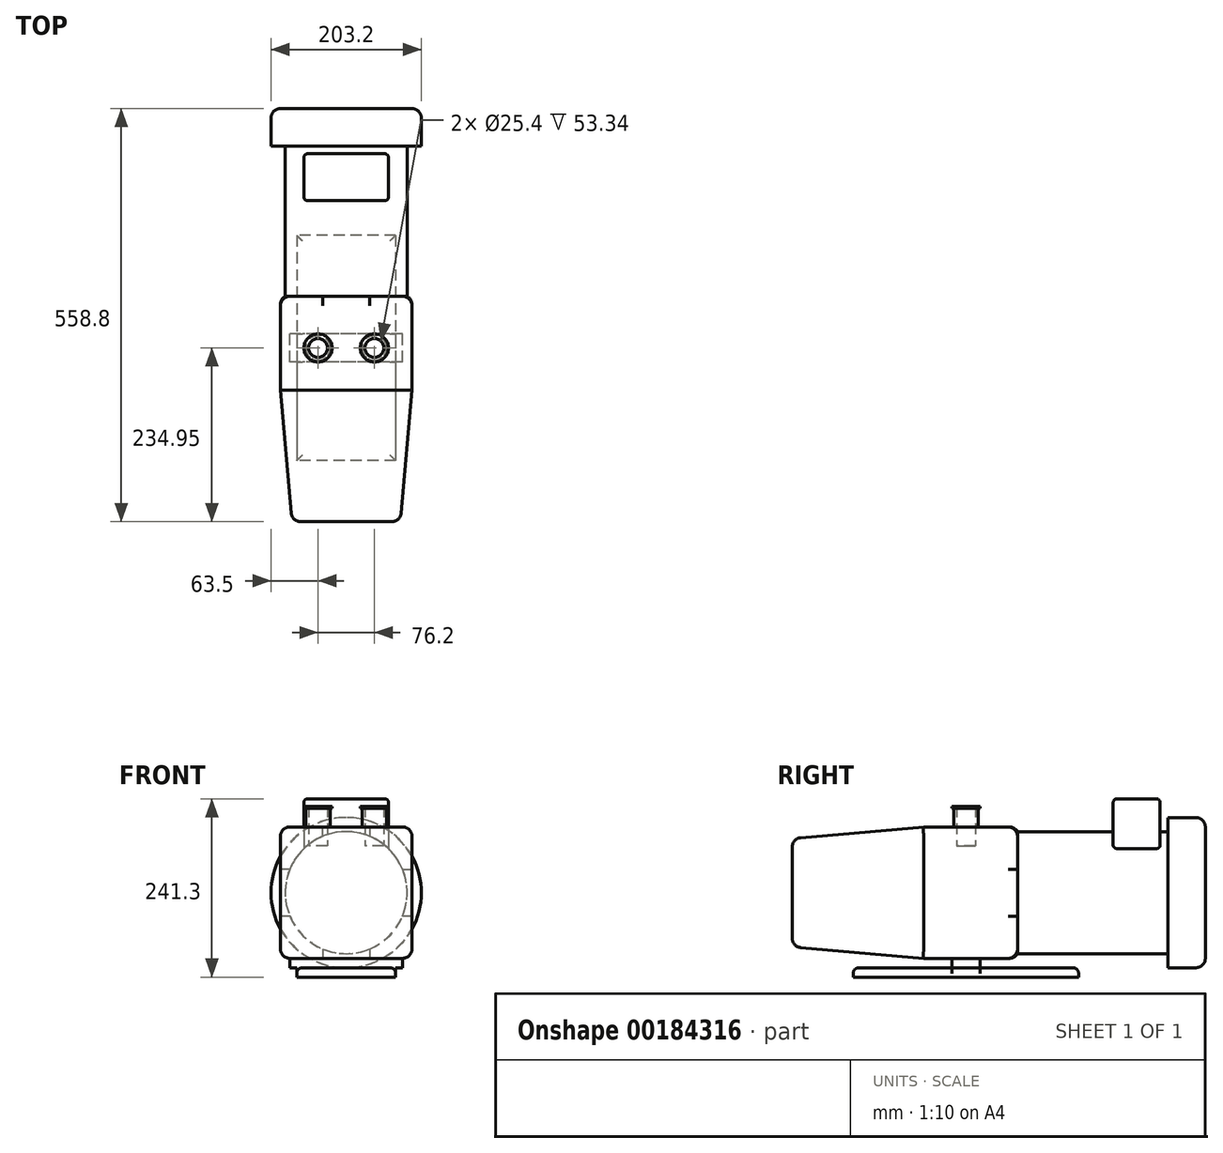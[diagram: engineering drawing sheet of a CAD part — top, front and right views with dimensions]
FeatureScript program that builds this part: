
annotation { "Feature Type Name" : "Feature", "Feature Type Description" : "" }
export const myFeature = defineFeature(function(context is Context, id is Id, definition is map)
    precondition{}
    {
        {
            var Q0;
            Q0=qCreatedBy(makeId("Front.planeOp"),FACE);
            var sketch = newSketch(context, id + "F0", { "sketchPlane" : qUnion([Q0])});
            skLineSegment(sketch, "E0.bottom", {"start": v(88.9, -88.9) * mm, "end": v(-88.9, -88.9) * mm});
            skLineSegment(sketch, "E0.top", {"start": v(88.9, 88.9) * mm, "end": v(-88.9, 88.9) * mm});
            skLineSegment(sketch, "E0.left", {"start": v(88.9, -88.9) * mm, "end": v(88.9, 88.9) * mm});
            skLineSegment(sketch, "E0.right", {"start": v(-88.9, -88.9) * mm, "end": v(-88.9, 88.9) * mm});
            skPoint(sketch, "E0.middle", {"position": v(0, 0) * mm});
            skSolve(sketch);
        }
        {
            var Q0;
            Q0=makeQuery(id+"F0.imprint","IMPRINT",FACE,{"disambiguationData":[TD([[makeQuery(id+"F0.imprint","IMPRINT",EDGE,{"derivedFrom":sQuery(id+"F0.wireOp",EDGE,"E0.bottom")}),-1.0]])]});
            extrude(context, id + "F1", {"entities" : qUnion([Q0]), "depth" : 127 * mm});
        }
        {
            var Q0;
            Q0=makeQuery(id+"F1.opExtrude","CAP_FACE",FACE,{"disambiguationData":[OSD([sQuery(id+"F0.wireOp",EDGE,"E0.bottom"),sQuery(id+"F0.wireOp",EDGE,"E0.top"),sQuery(id+"F0.wireOp",EDGE,"E0.left"),sQuery(id+"F0.wireOp",EDGE,"E0.right")])],"isStart":false});
            var sketch = newSketch(context, id + "F2", { "sketchPlane" : qUnion([Q0])});
            skLineSegment(sketch, "E1.bottom", {"start": v(88.9, -88.9) * mm, "end": v(-88.9, -88.9) * mm});
            skLineSegment(sketch, "E1.top", {"start": v(88.9, 88.9) * mm, "end": v(-88.9, 88.9) * mm});
            skLineSegment(sketch, "E1.left", {"start": v(88.9, -88.9) * mm, "end": v(88.9, 88.9) * mm});
            skLineSegment(sketch, "E1.right", {"start": v(-88.9, -88.9) * mm, "end": v(-88.9, 88.9) * mm});
            skPoint(sketch, "E1.middle", {"position": v(0, 0) * mm});
            skSolve(sketch);
        }
        {
            var Q0;
            Q0 = qSketchRegion(id + "F2", true);
            extrude(context, id + "F3", {"entities" : qUnion([Q0]), "operationType" : NewBodyOperationType.ADD, "depth" : 177.8 * mm, "hasDraft" : true, "draftAngle" : 5 * degree, "draftPullDirection" : true});
        }
        {
            var Q0;
            Q0=makeQuery(id+"F1.opExtrude","CAP_FACE",FACE,{"disambiguationData":[OSD([sQuery(id+"F0.wireOp",EDGE,"E0.bottom"),sQuery(id+"F0.wireOp",EDGE,"E0.top"),sQuery(id+"F0.wireOp",EDGE,"E0.left"),sQuery(id+"F0.wireOp",EDGE,"E0.right")])],"isStart":true});
            var sketch = newSketch(context, id + "F4", { "sketchPlane" : qUnion([Q0])});
            skCircle(sketch, "E2", {"center": v(0, 0) * mm, "radius": 82.55 * mm});
            skSolve(sketch);
        }
        {
            var Q0;
            Q0 = qSketchRegion(id + "F4", true);
            extrude(context, id + "F5", {"entities" : qUnion([Q0]), "operationType" : NewBodyOperationType.ADD, "depth" : 203.2 * mm});
        }
        {
            var Q0;
            Q0=makeQuery(id+"F5.opExtrude","CAP_FACE",FACE,{"disambiguationData":[OSD([sQuery(id+"F4.wireOp",EDGE,"E2")])],"isStart":false});
            var sketch = newSketch(context, id + "F6", { "sketchPlane" : qUnion([Q0])});
            skCircle(sketch, "E3", {"center": v(0, 0) * mm, "radius": 101.6 * mm});
            skSolve(sketch);
        }
        {
            var Q0;
            Q0 = qSketchRegion(id + "F6", true);
            extrude(context, id + "F7", {"entities" : qUnion([Q0]), "operationType" : NewBodyOperationType.ADD, "depth" : 50.8 * mm});
        }
        {
            var Q0;
            Q0=makeQuery(id+"F3.opExtrude","SWEPT_EDGE",EDGE,{"disambiguationData":[OSD([sQuery(id+"F2.wireOp",EDGE,"E1.top"),sQuery(id+"F2.wireOp",EDGE,"E1.left")])]});
            var Q1;
            Q1=makeQuery(id+"F3.opExtrude","SWEPT_EDGE",EDGE,{"disambiguationData":[OSD([sQuery(id+"F2.wireOp",EDGE,"E1.top"),sQuery(id+"F2.wireOp",EDGE,"E1.right")])]});
            var Q2;
            Q2=makeQuery(id+"F1.opExtrude","SWEPT_EDGE",EDGE,{"disambiguationData":[OSD([sQuery(id+"F0.wireOp",EDGE,"E0.top"),sQuery(id+"F0.wireOp",EDGE,"E0.left")])]});
            var Q3;
            Q3=makeQuery(id+"F1.opExtrude","CAP_EDGE",EDGE,{"disambiguationData":[OSD([sQuery(id+"F0.wireOp",EDGE,"E0.left")])],"isStart":true});
            var Q4;
            Q4=makeQuery(id+"F1.opExtrude","SWEPT_EDGE",EDGE,{"disambiguationData":[OSD([sQuery(id+"F0.wireOp",EDGE,"E0.bottom"),sQuery(id+"F0.wireOp",EDGE,"E0.left")])]});
            var Q5;
            Q5=makeQuery(id+"F3.opExtrude","SWEPT_EDGE",EDGE,{"disambiguationData":[OSD([sQuery(id+"F2.wireOp",EDGE,"E1.bottom"),sQuery(id+"F2.wireOp",EDGE,"E1.left")])]});
            var Q6;
            Q6=makeQuery(id+"F3.opExtrude","CAP_EDGE",EDGE,{"disambiguationData":[OSD([sQuery(id+"F2.wireOp",EDGE,"E1.left")])],"isStart":false});
            var Q7;
            Q7=makeQuery(id+"F3.opExtrude","CAP_EDGE",EDGE,{"disambiguationData":[OSD([sQuery(id+"F2.wireOp",EDGE,"E1.top")])],"isStart":false});
            var Q8;
            Q8=makeQuery(id+"F3.opExtrude","CAP_EDGE",EDGE,{"disambiguationData":[OSD([sQuery(id+"F2.wireOp",EDGE,"E1.right")])],"isStart":false});
            var Q9;
            Q9=makeQuery(id+"F3.opExtrude","CAP_EDGE",EDGE,{"disambiguationData":[OSD([sQuery(id+"F2.wireOp",EDGE,"E1.bottom")])],"isStart":false});
            var Q10;
            Q10=makeQuery(id+"F3.opExtrude","SWEPT_EDGE",EDGE,{"disambiguationData":[OSD([sQuery(id+"F2.wireOp",EDGE,"E1.bottom"),sQuery(id+"F2.wireOp",EDGE,"E1.right")])]});
            var Q11;
            Q11=makeQuery(id+"F1.opExtrude","CAP_EDGE",EDGE,{"disambiguationData":[OSD([sQuery(id+"F0.wireOp",EDGE,"E0.right")])],"isStart":true});
            var Q12;
            Q12=makeQuery(id+"F1.opExtrude","CAP_EDGE",EDGE,{"disambiguationData":[OSD([sQuery(id+"F0.wireOp",EDGE,"E0.top")])],"isStart":true});
            var Q13;
            Q13=makeQuery(id+"F1.opExtrude","SWEPT_EDGE",EDGE,{"disambiguationData":[OSD([sQuery(id+"F0.wireOp",EDGE,"E0.bottom"),sQuery(id+"F0.wireOp",EDGE,"E0.right")])]});
            var Q14;
            Q14=makeQuery(id+"F1.opExtrude","CAP_EDGE",EDGE,{"disambiguationData":[OSD([sQuery(id+"F0.wireOp",EDGE,"E0.bottom")])],"isStart":true});
            var Q15;
            Q15=makeQuery(id+"F1.opExtrude","SWEPT_EDGE",EDGE,{"disambiguationData":[OSD([sQuery(id+"F0.wireOp",EDGE,"E0.top"),sQuery(id+"F0.wireOp",EDGE,"E0.right")])]});
            fillet(context, id + "F8", {"entities" : qUnion([Q0, Q1, Q2, Q3, Q4, Q5, Q6, Q7, Q8, Q9, Q10, Q11, Q12, Q13, Q14, Q15]), "radius" : 12.7 * mm, "tangentPropagation" : true, "allowEdgeOverflow" : false});
        }
        {
            var Q0;
            Q0=makeQuery(id+"F7.opExtrude","CAP_EDGE",EDGE,{"disambiguationData":[OSD([sQuery(id+"F6.wireOp",EDGE,"E3")])],"isStart":false});
            fillet(context, id + "F9", {"entities" : qUnion([Q0]), "radius" : 12.7 * mm, "tangentPropagation" : true, "allowEdgeOverflow" : false});
        }
        {
            var Q0;
            Q0=makeQuery(id+"F1.opExtrude","SWEPT_FACE",FACE,{"disambiguationData":[OSD([sQuery(id+"F0.wireOp",EDGE,"E0.bottom")])]});
            var sketch = newSketch(context, id + "F10", { "sketchPlane" : qUnion([Q0])});
            skLineSegment(sketch, "E4.bottom", {"start": v(76.2, 50.8) * mm, "end": v(-76.2, 50.8) * mm});
            skLineSegment(sketch, "E4.top", {"start": v(76.2, 88.9) * mm, "end": v(-76.2, 88.9) * mm});
            skLineSegment(sketch, "E4.left", {"start": v(76.2, 50.8) * mm, "end": v(76.2, 88.9) * mm});
            skLineSegment(sketch, "E4.right", {"start": v(-76.2, 50.8) * mm, "end": v(-76.2, 88.9) * mm});
            skPoint(sketch, "E4.middle", {"position": v(0, 69.85) * mm});
            skSolve(sketch);
        }
        {
            var Q0;
            Q0 = qSketchRegion(id + "F10", true);
            extrude(context, id + "F11", {"entities" : qUnion([Q0]), "operationType" : NewBodyOperationType.ADD, "depth" : 12.7 * mm});
        }
        {
            var Q0;
            Q0=makeQuery(id+"F11.opExtrude","CAP_FACE",FACE,{"disambiguationData":[OSD([sQuery(id+"F10.wireOp",EDGE,"E4.bottom"),sQuery(id+"F10.wireOp",EDGE,"E4.top"),sQuery(id+"F10.wireOp",EDGE,"E4.left"),sQuery(id+"F10.wireOp",EDGE,"E4.right")])],"isStart":false});
            var sketch = newSketch(context, id + "F12", { "sketchPlane" : qUnion([Q0])});
            skLineSegment(sketch, "E5.bottom", {"start": v(66.88, -82.55) * mm, "end": v(-66.88, -82.55) * mm});
            skLineSegment(sketch, "E5.top", {"start": v(66.88, 222.25) * mm, "end": v(-66.88, 222.25) * mm});
            skLineSegment(sketch, "E5.left", {"start": v(66.88, -82.55) * mm, "end": v(66.88, 222.25) * mm});
            skLineSegment(sketch, "E5.right", {"start": v(-66.88, -82.55) * mm, "end": v(-66.88, 222.25) * mm});
            skPoint(sketch, "E5.middle", {"position": v(0, 69.85) * mm});
            skPoint(sketch, "E5.middle.positionSnap0", {"position": v(0, 88.9) * mm});
            skPoint(sketch, "E5.centerSnap0", {"position": v(0, 88.9) * mm});
            skSolve(sketch);
        }
        {
            var Q0;
            Q0 = qSketchRegion(id + "F12", true);
            extrude(context, id + "F13", {"entities" : qUnion([Q0]), "operationType" : NewBodyOperationType.ADD, "depth" : 12.7 * mm});
        }
        {
            var Q0;
            {var subQ0=sQuery(id+"F12.wireOp",EDGE,"E5.right");var subQ1=sQuery(id+"F12.wireOp",EDGE,"E5.bottom");var subQ2=sQuery(id+"F10.wireOp",EDGE,"E4.bottom");Q0=makeQuery(id+"F13.boolean.opBoolean","SPLIT",EDGE,{"disambiguationData":[TD([makeQuery(id+"F11.opExtrude","SWEPT_FACE",FACE,{"disambiguationData":[OSD([subQ2])]}),makeQuery(id+"F11.opExtrude","CAP_FACE",FACE,{"disambiguationData":[OSD([subQ2,sQuery(id+"F10.wireOp",EDGE,"E4.top"),sQuery(id+"F10.wireOp",EDGE,"E4.left"),sQuery(id+"F10.wireOp",EDGE,"E4.right")])],"isStart":false}),makeQuery(id+"F13.opExtrude","SWEPT_FACE",FACE,{"disambiguationData":[OSD([subQ1])]}),makeQuery(id+"F13.opExtrude","CAP_FACE",FACE,{"disambiguationData":[OSD([subQ1,sQuery(id+"F12.wireOp",EDGE,"E5.top"),sQuery(id+"F12.wireOp",EDGE,"E5.left"),subQ0])],"isStart":true}),makeQuery(id+"F13.opExtrude","SWEPT_FACE",FACE,{"disambiguationData":[OSD([subQ0])]})])],"derivedFrom":makeQuery(id+"F13.opExtrude","CAP_EDGE",EDGE,{"disambiguationData":[OSD([subQ0])],"isStart":true})});}
            var Q1;
            {var subQ0=sQuery(id+"F12.wireOp",EDGE,"E5.top");var subQ1=sQuery(id+"F12.wireOp",EDGE,"E5.right");var subQ2=sQuery(id+"F10.wireOp",EDGE,"E4.top");Q1=makeQuery(id+"F13.boolean.opBoolean","SPLIT",EDGE,{"disambiguationData":[TD([makeQuery(id+"F11.opExtrude","CAP_FACE",FACE,{"disambiguationData":[OSD([sQuery(id+"F10.wireOp",EDGE,"E4.bottom"),subQ2,sQuery(id+"F10.wireOp",EDGE,"E4.left"),sQuery(id+"F10.wireOp",EDGE,"E4.right")])],"isStart":false}),makeQuery(id+"F11.opExtrude","SWEPT_FACE",FACE,{"disambiguationData":[OSD([subQ2])]}),makeQuery(id+"F13.opExtrude","CAP_FACE",FACE,{"disambiguationData":[OSD([sQuery(id+"F12.wireOp",EDGE,"E5.bottom"),subQ0,sQuery(id+"F12.wireOp",EDGE,"E5.left"),subQ1])],"isStart":true}),makeQuery(id+"F13.opExtrude","SWEPT_FACE",FACE,{"disambiguationData":[OSD([subQ0])]}),makeQuery(id+"F13.opExtrude","SWEPT_FACE",FACE,{"disambiguationData":[OSD([subQ1])]})])],"derivedFrom":makeQuery(id+"F13.opExtrude","CAP_EDGE",EDGE,{"disambiguationData":[OSD([subQ1])],"isStart":true})});}
            var Q2;
            Q2=makeQuery(id+"F13.opExtrude","CAP_EDGE",EDGE,{"disambiguationData":[OSD([sQuery(id+"F12.wireOp",EDGE,"E5.bottom")])],"isStart":true});
            var Q3;
            Q3=makeQuery(id+"F13.opExtrude","CAP_EDGE",EDGE,{"disambiguationData":[OSD([sQuery(id+"F12.wireOp",EDGE,"E5.top")])],"isStart":true});
            var Q4;
            {var subQ0=sQuery(id+"F12.wireOp",EDGE,"E5.left");var subQ1=sQuery(id+"F12.wireOp",EDGE,"E5.bottom");var subQ2=sQuery(id+"F10.wireOp",EDGE,"E4.bottom");Q4=makeQuery(id+"F13.boolean.opBoolean","SPLIT",EDGE,{"disambiguationData":[TD([makeQuery(id+"F11.opExtrude","SWEPT_FACE",FACE,{"disambiguationData":[OSD([subQ2])]}),makeQuery(id+"F11.opExtrude","CAP_FACE",FACE,{"disambiguationData":[OSD([subQ2,sQuery(id+"F10.wireOp",EDGE,"E4.top"),sQuery(id+"F10.wireOp",EDGE,"E4.left"),sQuery(id+"F10.wireOp",EDGE,"E4.right")])],"isStart":false}),makeQuery(id+"F13.opExtrude","SWEPT_FACE",FACE,{"disambiguationData":[OSD([subQ1])]}),makeQuery(id+"F13.opExtrude","CAP_FACE",FACE,{"disambiguationData":[OSD([subQ1,sQuery(id+"F12.wireOp",EDGE,"E5.top"),subQ0,sQuery(id+"F12.wireOp",EDGE,"E5.right")])],"isStart":true}),makeQuery(id+"F13.opExtrude","SWEPT_FACE",FACE,{"disambiguationData":[OSD([subQ0])]})])],"derivedFrom":makeQuery(id+"F13.opExtrude","CAP_EDGE",EDGE,{"disambiguationData":[OSD([subQ0])],"isStart":true})});}
            var Q5;
            {var subQ0=sQuery(id+"F12.wireOp",EDGE,"E5.top");var subQ1=sQuery(id+"F12.wireOp",EDGE,"E5.left");var subQ2=sQuery(id+"F10.wireOp",EDGE,"E4.top");Q5=makeQuery(id+"F13.boolean.opBoolean","SPLIT",EDGE,{"disambiguationData":[TD([makeQuery(id+"F11.opExtrude","CAP_FACE",FACE,{"disambiguationData":[OSD([sQuery(id+"F10.wireOp",EDGE,"E4.bottom"),subQ2,sQuery(id+"F10.wireOp",EDGE,"E4.left"),sQuery(id+"F10.wireOp",EDGE,"E4.right")])],"isStart":false}),makeQuery(id+"F11.opExtrude","SWEPT_FACE",FACE,{"disambiguationData":[OSD([subQ2])]}),makeQuery(id+"F13.opExtrude","CAP_FACE",FACE,{"disambiguationData":[OSD([sQuery(id+"F12.wireOp",EDGE,"E5.bottom"),subQ0,subQ1,sQuery(id+"F12.wireOp",EDGE,"E5.right")])],"isStart":true}),makeQuery(id+"F13.opExtrude","SWEPT_FACE",FACE,{"disambiguationData":[OSD([subQ0])]}),makeQuery(id+"F13.opExtrude","SWEPT_FACE",FACE,{"disambiguationData":[OSD([subQ1])]})])],"derivedFrom":makeQuery(id+"F13.opExtrude","CAP_EDGE",EDGE,{"disambiguationData":[OSD([subQ1])],"isStart":true})});}
            fillet(context, id + "F14", {"entities" : qUnion([Q0, Q1, Q2, Q3, Q4, Q5]), "radius" : 7.62 * mm, "tangentPropagation" : true, "allowEdgeOverflow" : false});
        }
        {
            var Q0;
            Q0=qCreatedBy(makeId("Top.planeOp"),FACE);
            cPlane(context, id + "F15", {"entities" : qUnion([Q0]), "cplaneType" : CPlaneType.OFFSET, "offset" : 101.6 * mm, "width" : 152.4 * mm, "height" : 152.4 * mm});
        }
        {
            var Q0;
            Q0=qCreatedBy(id+"F15.planeOp",FACE);
            var sketch = newSketch(context, id + "F16", { "sketchPlane" : qUnion([Q0])});
            skLineSegment(sketch, "E6.bottom", {"start": v(57.15, 129.34) * mm, "end": v(-57.15, 129.34) * mm});
            skLineSegment(sketch, "E6.top", {"start": v(57.15, 192.84) * mm, "end": v(-57.15, 192.84) * mm});
            skLineSegment(sketch, "E6.left", {"start": v(57.15, 129.34) * mm, "end": v(57.15, 192.84) * mm});
            skLineSegment(sketch, "E6.right", {"start": v(-57.15, 129.34) * mm, "end": v(-57.15, 192.84) * mm});
            skPoint(sketch, "E6.middle", {"position": v(0, 161.09) * mm});
            skSolve(sketch);
        }
        {
            var Q0;
            Q0 = qSketchRegion(id + "F16", true);
            extrude(context, id + "F17", {"entities" : qUnion([Q0]), "operationType" : NewBodyOperationType.ADD, "depth" : 25.4 * mm, "hasSecondDirection" : true, "secondDirectionOppositeDirection" : true, "secondDirectionDepth" : 50.8 * mm});
        }
        {
            var Q0;
            Q0=makeQuery(id+"F17.opExtrude","CAP_EDGE",EDGE,{"disambiguationData":[OSD([sQuery(id+"F16.wireOp",EDGE,"E6.right")])],"isStart":false});
            var Q1;
            Q1=makeQuery(id+"F17.opExtrude","CAP_EDGE",EDGE,{"disambiguationData":[OSD([sQuery(id+"F16.wireOp",EDGE,"E6.bottom")])],"isStart":false});
            var Q2;
            Q2=makeQuery(id+"F17.opExtrude","CAP_EDGE",EDGE,{"disambiguationData":[OSD([sQuery(id+"F16.wireOp",EDGE,"E6.top")])],"isStart":false});
            var Q3;
            Q3=makeQuery(id+"F17.opExtrude","CAP_EDGE",EDGE,{"disambiguationData":[OSD([sQuery(id+"F16.wireOp",EDGE,"E6.left")])],"isStart":false});
            var Q4;
            Q4=makeQuery(id+"F17.opExtrude","SWEPT_EDGE",EDGE,{"disambiguationData":[OSD([sQuery(id+"F16.wireOp",EDGE,"E6.bottom"),sQuery(id+"F16.wireOp",EDGE,"E6.right")])]});
            var Q5;
            Q5=makeQuery(id+"F17.opExtrude","SWEPT_EDGE",EDGE,{"disambiguationData":[OSD([sQuery(id+"F16.wireOp",EDGE,"E6.bottom"),sQuery(id+"F16.wireOp",EDGE,"E6.left")])]});
            var Q6;
            Q6=makeQuery(id+"F17.opExtrude","SWEPT_EDGE",EDGE,{"disambiguationData":[OSD([sQuery(id+"F16.wireOp",EDGE,"E6.top"),sQuery(id+"F16.wireOp",EDGE,"E6.right")])]});
            var Q7;
            Q7=makeQuery(id+"F17.opExtrude","SWEPT_EDGE",EDGE,{"disambiguationData":[OSD([sQuery(id+"F16.wireOp",EDGE,"E6.top"),sQuery(id+"F16.wireOp",EDGE,"E6.left")])]});
            fillet(context, id + "F18", {"entities" : qUnion([Q0, Q1, Q2, Q3, Q4, Q5, Q6, Q7]), "radius" : 5.08 * mm, "tangentPropagation" : true, "allowEdgeOverflow" : false});
        }
        {
            var Q0;
            Q0=makeQuery(id+"F1.opExtrude","SWEPT_FACE",FACE,{"disambiguationData":[OSD([sQuery(id+"F0.wireOp",EDGE,"E0.top")])]});
            var sketch = newSketch(context, id + "F19", { "sketchPlane" : qUnion([Q0])});
            skLineSegment(sketch, "E7", {"start": v(-76.2, -69.85) * mm, "end": v(76.2, -69.85) * mm, "construction": true});
            skLineSegment(sketch, "E8", {"start": v(0, -127) * mm, "end": v(0, -11) * mm, "construction": true});
            skPoint(sketch, "E9", {"position": v(0, -69.85) * mm});
            skPoint(sketch, "E10", {"position": v(-38.1, -69.85) * mm});
            skPoint(sketch, "E11.MirrorP", {"position": v(38.1, -69.85) * mm});
            skCircle(sketch, "E12", {"center": v(-38.1, -69.85) * mm, "radius": 12.7 * mm});
            skCircle(sketch, "E13", {"center": v(38.1, -69.85) * mm, "radius": 12.7 * mm});
            skCircle(sketch, "E14", {"center": v(-38.1, -69.85) * mm, "radius": 16.51 * mm});
            skCircle(sketch, "E15", {"center": v(38.1, -69.85) * mm, "radius": 16.51 * mm});
            skSolve(sketch);
        }
        {
            var Q0;
            Q0 = qSketchRegion(id + "F19", true);
            extrude(context, id + "F20", {"entities" : qUnion([Q0]), "operationType" : NewBodyOperationType.ADD, "depth" : 25.4 * mm});
        }
        {
            var Q0;
            Q0=makeQuery(id+"F20.opExtrude","CAP_FACE",FACE,{"disambiguationData":[OSD([sQuery(id+"F19.wireOp",EDGE,"E12"),sQuery(id+"F19.wireOp",EDGE,"E14")])],"isStart":false});
            var sketch = newSketch(context, id + "F21", { "sketchPlane" : qUnion([Q0])});
            skCircle(sketch, "E16", {"center": v(-38.1, -69.85) * mm, "radius": 19.05 * mm});
            skCircle(sketch, "E17.MirrorC", {"center": v(38.1, -69.85) * mm, "radius": 19.05 * mm});
            skCircle(sketch, "E18", {"center": v(-38.1, -69.85) * mm, "radius": 12.7 * mm});
            skCircle(sketch, "E19", {"center": v(38.1, -69.85) * mm, "radius": 12.7 * mm});
            skSolve(sketch);
        }
        {
            var Q0;
            Q0 = qSketchRegion(id + "F21", true);
            extrude(context, id + "F22", {"entities" : qUnion([Q0]), "operationType" : NewBodyOperationType.ADD, "depth" : 2.54 * mm});
        }
        {
            var Q0;
            Q0=makeQuery(id+"F19.imprint","IMPRINT",FACE,{"disambiguationData":[TD([[makeQuery(id+"F19.imprint","IMPRINT",EDGE,{"derivedFrom":sQuery(id+"F19.wireOp",EDGE,"E12")}),1.0]])]});
            var Q1;
            Q1=makeQuery(id+"F19.imprint","IMPRINT",FACE,{"disambiguationData":[TD([[makeQuery(id+"F19.imprint","IMPRINT",EDGE,{"derivedFrom":sQuery(id+"F19.wireOp",EDGE,"E13")}),1.0]])]});
            extrude(context, id + "F23", {"entities" : qUnion([Q0, Q1]), "operationType" : NewBodyOperationType.REMOVE, "oppositeDirection" : true, "depth" : 25.4 * mm});
        }
    });
